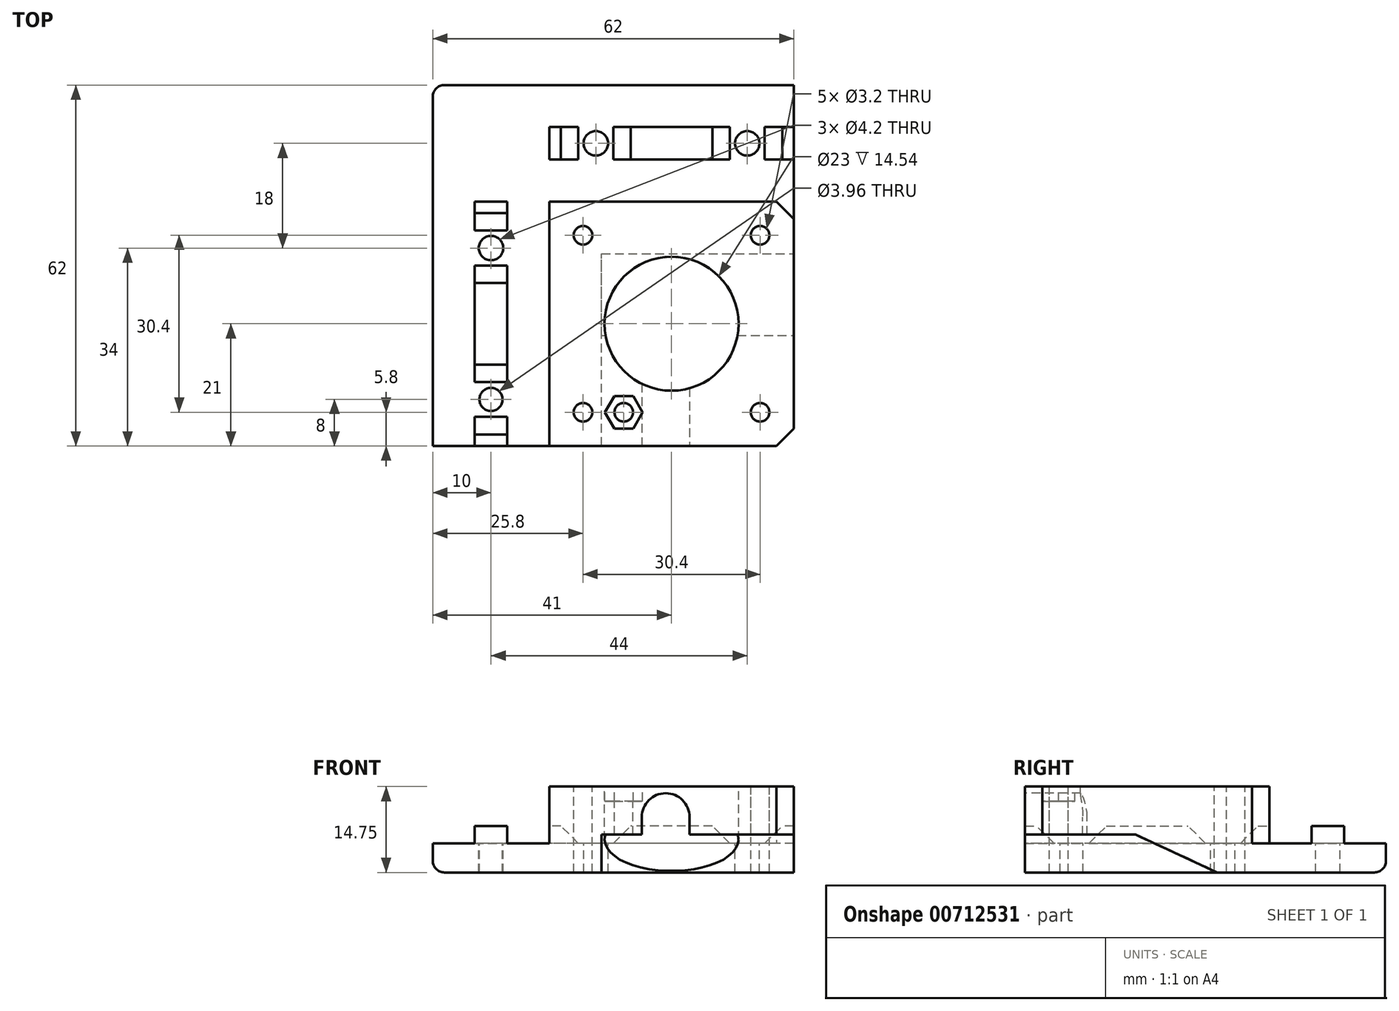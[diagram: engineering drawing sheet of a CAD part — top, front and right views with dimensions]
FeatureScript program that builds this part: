
annotation { "Feature Type Name" : "Feature", "Feature Type Description" : "" }
export const myFeature = defineFeature(function(context is Context, id is Id, definition is map)
    precondition{}
    {
        {
            var Q0;
            Q0=qCreatedBy(makeId("Top.planeOp"),FACE);
            var sketch = newSketch(context, id + "F0", { "sketchPlane" : qUnion([Q0])});
            skLineSegment(sketch, "E0.bottom", {"start": v(0, 0) * mm, "end": v(59, 0) * mm});
            skLineSegment(sketch, "E0.top", {"start": v(0, 54) * mm, "end": v(59, 54) * mm});
            skLineSegment(sketch, "E0.left", {"start": v(0, 0) * mm, "end": v(0, 54) * mm});
            skLineSegment(sketch, "E0.right", {"start": v(59, 0) * mm, "end": v(59, 54) * mm});
            skSolve(sketch);
        }
        {
            var Q0;
            Q0=makeQuery(id+"F0.imprint","IMPRINT",FACE,{"disambiguationData":[TD([[makeQuery(id+"F0.imprint","IMPRINT",EDGE,{"derivedFrom":sQuery(id+"F0.wireOp",EDGE,"E0.bottom")}),1.0]])]});
            extrude(context, id + "F1", {"entities" : qUnion([Q0]), "depth" : 5 * mm, "offsetDistance" : 25 * mm});
        }
        {
            var Q0;
            Q0=makeQuery(id+"F1.opExtrude","CAP_FACE",FACE,{"disambiguationData":[OSD([sQuery(id+"F0.wireOp",EDGE,"E0.bottom"),sQuery(id+"F0.wireOp",EDGE,"E0.top"),sQuery(id+"F0.wireOp",EDGE,"E0.left"),sQuery(id+"F0.wireOp",EDGE,"E0.right")])],"isStart":false});
            var sketch = newSketch(context, id + "F2", { "sketchPlane" : qUnion([Q0])});
            skLineSegment(sketch, "E1.bottom", {"start": v(59, 0) * mm, "end": v(17, 0) * mm});
            skLineSegment(sketch, "E1.top", {"start": v(59, 42) * mm, "end": v(17, 42) * mm});
            skLineSegment(sketch, "E1.left", {"start": v(59, 0) * mm, "end": v(59, 42) * mm});
            skLineSegment(sketch, "E1.right", {"start": v(17, 0) * mm, "end": v(17, 42) * mm});
            skSolve(sketch);
        }
        {
            var Q0;
            Q0=makeQuery(id+"F2.imprint","IMPRINT",FACE,{"disambiguationData":[TD([[makeQuery(id+"F2.imprint","IMPRINT",EDGE,{"derivedFrom":sQuery(id+"F2.wireOp",EDGE,"E1.bottom")}),1.0]])]});
            extrude(context, id + "F3", {"entities" : qUnion([Q0]), "operationType" : NewBodyOperationType.ADD, "depth" : 9.75 * mm, "offsetDistance" : 25 * mm});
        }
        {
            var Q0;
            Q0=makeQuery(id+"F3.boolean.opBoolean","MERGE",FACE,{"derivedFrom":[makeQuery(id+"F1.opExtrude","SWEPT_FACE",FACE,{"disambiguationData":[OSD([sQuery(id+"F0.wireOp",EDGE,"E0.right")])]}),makeQuery(id+"F3.opExtrude","SWEPT_FACE",FACE,{"disambiguationData":[OSD([sQuery(id+"F2.wireOp",EDGE,"E1.left")])]})]});
            var sketch = newSketch(context, id + "F4", { "sketchPlane" : qUnion([Q0])});
            skLineSegment(sketch, "E2", {"start": v(0, 0) * mm, "end": v(0, 6.5) * mm});
            skLineSegment(sketch, "E3", {"start": v(0, 6.5) * mm, "end": v(19, 6.5) * mm});
            skLineSegment(sketch, "E4", {"start": v(19, 6.5) * mm, "end": v(33, 0) * mm});
            skLineSegment(sketch, "E5", {"start": v(33, 0) * mm, "end": v(0, 0) * mm});
            skSolve(sketch);
        }
        {
            var Q0;
            Q0=makeQuery(id+"F4.imprint","IMPRINT",FACE,{"disambiguationData":[TD([[makeQuery(id+"F4.imprint","IMPRINT",EDGE,{"derivedFrom":sQuery(id+"F4.wireOp",EDGE,"E2")}),1.0]])]});
            extrude(context, id + "F5", {"entities" : qUnion([Q0]), "operationType" : NewBodyOperationType.REMOVE, "oppositeDirection" : true, "depth" : 33 * mm, "offsetDistance" : 25 * mm});
        }
        {
            var Q0;
            Q0=makeQuery(id+"F3.opExtrude","CAP_FACE",FACE,{"disambiguationData":[OSD([sQuery(id+"F2.wireOp",EDGE,"E1.bottom"),sQuery(id+"F2.wireOp",EDGE,"E1.top"),sQuery(id+"F2.wireOp",EDGE,"E1.left"),sQuery(id+"F2.wireOp",EDGE,"E1.right")])],"isStart":false});
            var sketch = newSketch(context, id + "F6", { "sketchPlane" : qUnion([Q0])});
            skCircle(sketch, "E6", {"center": v(38, 21) * mm, "radius": 11.5 * mm});
            skCircle(sketch, "E7", {"center": v(22.8, 36.2) * mm, "radius": 1.6 * mm});
            skCircle(sketch, "E8", {"center": v(53.2, 36.2) * mm, "radius": 1.6 * mm});
            skCircle(sketch, "E9", {"center": v(22.8, 5.8) * mm, "radius": 1.6 * mm});
            skCircle(sketch, "E10", {"center": v(53.2, 5.8) * mm, "radius": 1.6 * mm});
            skCircle(sketch, "E11", {"center": v(29.8, 5.8) * mm, "radius": 1.6 * mm});
            skSolve(sketch);
        }
        {
            var Q0;
            Q0=makeQuery(id+"F6.imprint","IMPRINT",FACE,{"disambiguationData":[TD([[makeQuery(id+"F6.imprint","IMPRINT",EDGE,{"derivedFrom":sQuery(id+"F6.wireOp",EDGE,"E7")}),1.0]])]});
            var Q1;
            Q1=makeQuery(id+"F6.imprint","IMPRINT",FACE,{"disambiguationData":[TD([[makeQuery(id+"F6.imprint","IMPRINT",EDGE,{"derivedFrom":sQuery(id+"F6.wireOp",EDGE,"E6")}),1.0]])]});
            var Q2;
            Q2=makeQuery(id+"F6.imprint","IMPRINT",FACE,{"disambiguationData":[TD([[makeQuery(id+"F6.imprint","IMPRINT",EDGE,{"derivedFrom":sQuery(id+"F6.wireOp",EDGE,"E8")}),1.0]])]});
            var Q3;
            Q3=makeQuery(id+"F6.imprint","IMPRINT",FACE,{"disambiguationData":[TD([[makeQuery(id+"F6.imprint","IMPRINT",EDGE,{"derivedFrom":sQuery(id+"F6.wireOp",EDGE,"E9")}),1.0]])]});
            var Q4;
            Q4=makeQuery(id+"F6.imprint","IMPRINT",FACE,{"disambiguationData":[TD([[makeQuery(id+"F6.imprint","IMPRINT",EDGE,{"derivedFrom":sQuery(id+"F6.wireOp",EDGE,"E10")}),1.0]])]});
            var Q5;
            Q5=makeQuery(id+"F6.imprint","IMPRINT",FACE,{"disambiguationData":[TD([[makeQuery(id+"F6.imprint","IMPRINT",EDGE,{"derivedFrom":sQuery(id+"F6.wireOp",EDGE,"E11")}),1.0]])]});
            extrude(context, id + "F7", {"entities" : qUnion([Q0, Q1, Q2, Q3, Q4, Q5]), "operationType" : NewBodyOperationType.REMOVE, "endBound" : BoundingType.THROUGH_ALL, "oppositeDirection" : true, "depth" : 25 * mm, "offsetDistance" : 25 * mm});
        }
        {
            var Q0;
            Q0=makeQuery(id+"F3.opExtrude","SWEPT_EDGE",EDGE,{"disambiguationData":[OSD([sQuery(id+"F0.wireOp",EDGE,"E0.right"),sQuery(id+"F2.wireOp",EDGE,"E1.top"),sQuery(id+"F2.wireOp",EDGE,"E1.left")])]});
            var Q1;
            Q1=makeQuery(id+"F3.boolean.opBoolean","MERGE",EDGE,{"derivedFrom":[makeQuery(id+"F1.opExtrude","SWEPT_EDGE",EDGE,{"disambiguationData":[OSD([sQuery(id+"F0.wireOp",EDGE,"E0.bottom"),sQuery(id+"F0.wireOp",EDGE,"E0.right")])]}),makeQuery(id+"F3.opExtrude","SWEPT_EDGE",EDGE,{"disambiguationData":[OSD([sQuery(id+"F2.wireOp",EDGE,"E1.bottom"),sQuery(id+"F2.wireOp",EDGE,"E1.left")])]})]});
            chamfer(context, id + "F8", {"entities" : qUnion([Q0, Q1]), "width" : 3 * mm, "tangentPropagation" : true});
        }
        {
            var Q0;
            Q0=makeQuery(id+"F3.opExtrude","CAP_FACE",FACE,{"disambiguationData":[OSD([sQuery(id+"F2.wireOp",EDGE,"E1.bottom"),sQuery(id+"F2.wireOp",EDGE,"E1.top"),sQuery(id+"F2.wireOp",EDGE,"E1.left"),sQuery(id+"F2.wireOp",EDGE,"E1.right")])],"isStart":false});
            var sketch = newSketch(context, id + "F9", { "sketchPlane" : qUnion([Q0])});
            skCircle(sketch, "E12.cCircle", {"center": v(29.8, 5.8) * mm, "radius": 2.8 * mm, "construction": true});
            skLineSegment(sketch, "E12.0", {"start": v(33.03, 5.8) * mm, "end": v(31.42, 3) * mm});
            skLineSegment(sketch, "E12.1", {"start": v(31.42, 3) * mm, "end": v(28.18, 3) * mm});
            skLineSegment(sketch, "E12.2", {"start": v(28.18, 3) * mm, "end": v(26.57, 5.8) * mm});
            skLineSegment(sketch, "E12.3", {"start": v(26.57, 5.8) * mm, "end": v(28.18, 8.6) * mm});
            skLineSegment(sketch, "E12.4", {"start": v(28.18, 8.6) * mm, "end": v(31.42, 8.6) * mm});
            skLineSegment(sketch, "E12.5", {"start": v(31.42, 8.6) * mm, "end": v(33.03, 5.8) * mm});
            skPoint(sketch, "E12.0.midPoint", {"position": v(32.23, 4.4) * mm});
            skSolve(sketch);
        }
        {
            var Q0;
            Q0=makeQuery(id+"F9.imprint","IMPRINT",FACE,{"disambiguationData":[TD([[makeQuery(id+"F9.imprint","IMPRINT",EDGE,{"derivedFrom":sQuery(id+"F9.wireOp",EDGE,"E12.0")}),-1.0]])]});
            extrude(context, id + "F10", {"entities" : qUnion([Q0]), "operationType" : NewBodyOperationType.REMOVE, "oppositeDirection" : true, "depth" : 2.5 * mm, "offsetDistance" : 25 * mm});
        }
        {
            var Q0;
            Q0=makeQuery(id+"F3.boolean.opBoolean","MERGE",FACE,{"derivedFrom":[makeQuery(id+"F7aVUtGTQ7vZGl7_1.boolean.opBoolean","MERGE",FACE,{"derivedFrom":[makeQuery(id+"F1.opExtrude","SWEPT_FACE",FACE,{"disambiguationData":[OSD([sQuery(id+"F0.wireOp",EDGE,"E0.bottom")])]}),makeQuery(id+"F7aVUtGTQ7vZGl7_1.opExtrude","SWEPT_FACE",FACE,{"disambiguationData":[OSD([sQuery(id+"Fs2P3l27It3FXby_1.wireOp",EDGE,"bHcCaI8n-BMMI-Yc99-4eW4-bQ5ukSnPJtkv.top")])]})]}),makeQuery(id+"F3.opExtrude","SWEPT_FACE",FACE,{"disambiguationData":[OSD([sQuery(id+"F2.wireOp",EDGE,"E1.bottom")])]})]});
            var sketch = newSketch(context, id + "F11", { "sketchPlane" : qUnion([Q0])});
            skLineSegment(sketch, "E13.top", {"start": v(32.9, 6.5) * mm, "end": v(41.1, 6.5) * mm});
            skLineSegment(sketch, "E13.left", {"start": v(32.9, 9.5) * mm, "end": v(32.9, 6.5) * mm});
            skLineSegment(sketch, "E13.right", {"start": v(41.1, 9.5) * mm, "end": v(41.1, 6.5) * mm});
            skArc(sketch, "E14.trimOffspring", {"start": v(41.1, 9.5) * mm, "mid": v(37, 13.6) * mm, "end": v(32.9, 9.5) * mm});
            skSolve(sketch);
        }
        {
            var Q0;
            Q0=makeQuery(id+"F11.imprint","IMPRINT",FACE,{"disambiguationData":[TD([[makeQuery(id+"F11.imprint","IMPRINT",EDGE,{"derivedFrom":sQuery(id+"F11.wireOp",EDGE,"E13.top")}),1.0]])]});
            extrude(context, id + "F12", {"entities" : qUnion([Q0]), "operationType" : NewBodyOperationType.REMOVE, "endBound" : BoundingType.UP_TO_NEXT, "oppositeDirection" : true, "depth" : 25 * mm, "offsetDistance" : 25 * mm});
        }
        {
            var Q0;
            Q0=makeQuery(id+"F1.opExtrude","CAP_FACE",FACE,{"disambiguationData":[OSD([sQuery(id+"F0.wireOp",EDGE,"E0.bottom"),sQuery(id+"F0.wireOp",EDGE,"E0.top"),sQuery(id+"F0.wireOp",EDGE,"E0.left"),sQuery(id+"F0.wireOp",EDGE,"E0.right")])],"isStart":false});
            var sketch = newSketch(context, id + "F13", { "sketchPlane" : qUnion([Q0])});
            skLineSegment(sketch, "E15", {"start": v(56, 42) * mm, "end": v(59, 42) * mm});
            skSolve(sketch);
        }
        {
            var Q0;
            {var subQ1=sQuery(id+"F13.wireOp",EDGE,"E15");Q0=makeQuery(id+"F13.imprint","IMPRINT",FACE,{"disambiguationData":[TD([[makeQuery(id+"F13.imprint","IMPRINT",EDGE,{"derivedFrom":subQ1}),1.0]])]});}
            extrude(context, id + "F14", {"entities" : qUnion([Q0]), "operationType" : NewBodyOperationType.REMOVE, "endBound" : BoundingType.THROUGH_ALL, "oppositeDirection" : true, "depth" : 25 * mm, "offsetDistance" : 25 * mm});
        }
        {
            var Q0;
            {var subQ0=sQuery(id+"F2.wireOp",EDGE,"E1.top");Q0=makeQuery(id+"F14.boolean.opBoolean","MERGE",FACE,{"derivedFrom":[makeQuery(id+"F3.opExtrude","SWEPT_FACE",FACE,{"disambiguationData":[OSD([subQ0])]})],"fromTools":[makeQuery(id+"F14.opExtrude","SWEPT_FACE",FACE,{"disambiguationData":[OSD([subQ0,sQuery(id+"F13.wireOp",EDGE,"E15")])]})]});}
            var sketch = newSketch(context, id + "F15", { "sketchPlane" : qUnion([Q0])});
            skLineSegment(sketch, "E16.bottom", {"start": v(-59, 5) * mm, "end": v(-17, 5) * mm});
            skLineSegment(sketch, "E16.top", {"start": v(-59, 0) * mm, "end": v(-17, 0) * mm});
            skLineSegment(sketch, "E16.left", {"start": v(-59, 5) * mm, "end": v(-59, 0) * mm});
            skLineSegment(sketch, "E16.right", {"start": v(-17, 5) * mm, "end": v(-17, 0) * mm});
            skSolve(sketch);
        }
        {
            var Q0;
            Q0=makeQuery(id+"F15.imprint","IMPRINT",FACE,{"disambiguationData":[TD([[makeQuery(id+"F15.imprint","IMPRINT",EDGE,{"derivedFrom":sQuery(id+"F15.wireOp",EDGE,"E16.top")}),1.0]])]});
            extrude(context, id + "F16", {"entities" : qUnion([Q0]), "operationType" : NewBodyOperationType.ADD, "depth" : 20 * mm, "offsetDistance" : 25 * mm});
        }
        {
            var Q0;
            {var subQ0=sQuery(id+"F2.wireOp",EDGE,"E1.right");Q0=makeQuery(id+"F16.boolean.opBoolean","MERGE",FACE,{"derivedFrom":[makeQuery(id+"F14.boolean.opBoolean","MERGE",FACE,{"derivedFrom":[makeQuery(id+"F3.opExtrude","SWEPT_FACE",FACE,{"disambiguationData":[OSD([subQ0])]})],"fromTools":[makeQuery(id+"F14.opExtrude","SWEPT_FACE",FACE,{"disambiguationData":[OSD([subQ0])]})]}),makeQuery(id+"F16.opExtrude","SWEPT_FACE",FACE,{"disambiguationData":[OSD([sQuery(id+"F15.wireOp",EDGE,"E16.right")])]})]});}
            var sketch = newSketch(context, id + "F17", { "sketchPlane" : qUnion([Q0])});
            skLineSegment(sketch, "E17.bottom", {"start": v(-62, 5) * mm, "end": v(0, 5) * mm});
            skLineSegment(sketch, "E17.top", {"start": v(-62, 0) * mm, "end": v(0, 0) * mm});
            skLineSegment(sketch, "E17.left", {"start": v(-62, 5) * mm, "end": v(-62, 0) * mm});
            skLineSegment(sketch, "E17.right", {"start": v(0, 5) * mm, "end": v(0, 0) * mm});
            skSolve(sketch);
        }
        {
            var Q0;
            Q0=makeQuery(id+"F17.imprint","IMPRINT",FACE,{"disambiguationData":[TD([[makeQuery(id+"F17.imprint","IMPRINT",EDGE,{"derivedFrom":sQuery(id+"F17.wireOp",EDGE,"E17.top")}),-1.0]])]});
            extrude(context, id + "F18", {"entities" : qUnion([Q0]), "operationType" : NewBodyOperationType.ADD, "depth" : 20 * mm, "offsetDistance" : 25 * mm});
        }
        {
            var Q0;
            Q0=makeQuery(id+"F18.opExtrude","CAP_EDGE",EDGE,{"disambiguationData":[OSD([sQuery(id+"F17.wireOp",EDGE,"E17.left")])],"isStart":false});
            var Q1;
            Q1=makeQuery(id+"F18.opExtrude","CAP_EDGE",EDGE,{"disambiguationData":[OSD([sQuery(id+"F17.wireOp",EDGE,"E17.top")])],"isStart":false});
            var Q2;
            Q2=makeQuery(id+"F18.boolean.opBoolean","MERGE",EDGE,{"derivedFrom":[makeQuery(id+"F16.opExtrude","CAP_EDGE",EDGE,{"disambiguationData":[OSD([sQuery(id+"F15.wireOp",EDGE,"E16.top")])],"isStart":false}),makeQuery(id+"F18.opExtrude","SWEPT_EDGE",EDGE,{"disambiguationData":[OSD([sQuery(id+"F17.wireOp",EDGE,"E17.top"),sQuery(id+"F17.wireOp",EDGE,"E17.left")])]})]});
            fillet(context, id + "F19", {"entities" : qUnion([Q0, Q1, Q2]), "tangentPropagation" : true, "radius" : 2 * mm, "defaultsChanged" : false, "vertexSettings" : [], "allowEdgeOverflow" : false});
        }
        {
            var Q0;
            Q0=makeQuery(id+"F18.boolean.opBoolean","MERGE",FACE,{"derivedFrom":[makeQuery(id+"F16.boolean.opBoolean","MERGE",FACE,{"derivedFrom":[makeQuery(id+"F1.opExtrude","CAP_FACE",FACE,{"disambiguationData":[OSD([sQuery(id+"F0.wireOp",EDGE,"E0.bottom"),sQuery(id+"F0.wireOp",EDGE,"E0.top"),sQuery(id+"F0.wireOp",EDGE,"E0.left"),sQuery(id+"F0.wireOp",EDGE,"E0.right")])],"isStart":false}),makeQuery(id+"F16.opExtrude","SWEPT_FACE",FACE,{"disambiguationData":[OSD([sQuery(id+"F15.wireOp",EDGE,"E16.bottom")])]})]}),makeQuery(id+"F18.opExtrude","SWEPT_FACE",FACE,{"disambiguationData":[OSD([sQuery(id+"F17.wireOp",EDGE,"E17.bottom")])]})]});
            var sketch = newSketch(context, id + "F20", { "sketchPlane" : qUnion([Q0])});
            skLineSegment(sketch, "E18.bottom", {"start": v(59, 54.8) * mm, "end": v(17, 54.8) * mm});
            skLineSegment(sketch, "E18.top", {"start": v(59, 49.2) * mm, "end": v(17, 49.2) * mm});
            skLineSegment(sketch, "E18.left", {"start": v(59, 54.8) * mm, "end": v(59, 49.2) * mm});
            skLineSegment(sketch, "E18.right", {"start": v(17, 54.8) * mm, "end": v(17, 49.2) * mm});
            skLineSegment(sketch, "E19.bottom", {"start": v(4.2, 0) * mm, "end": v(9.8, 0) * mm});
            skLineSegment(sketch, "E19.top", {"start": v(4.2, 42) * mm, "end": v(9.8, 42) * mm});
            skLineSegment(sketch, "E19.left", {"start": v(4.2, 0) * mm, "end": v(4.2, 42) * mm});
            skLineSegment(sketch, "E19.right", {"start": v(9.8, 0) * mm, "end": v(9.8, 42) * mm});
            skLineSegment(sketch, "E20.bottom", {"start": v(22, 54.8) * mm, "end": v(28, 54.8) * mm});
            skLineSegment(sketch, "E20.top", {"start": v(22, 49.2) * mm, "end": v(28, 49.2) * mm});
            skLineSegment(sketch, "E20.left", {"start": v(22, 54.8) * mm, "end": v(22, 49.2) * mm});
            skLineSegment(sketch, "E20.right", {"start": v(28, 54.8) * mm, "end": v(28, 49.2) * mm});
            skLineSegment(sketch, "E21.bottom", {"start": v(48, 54.8) * mm, "end": v(54, 54.8) * mm});
            skLineSegment(sketch, "E21.top", {"start": v(48, 49.2) * mm, "end": v(54, 49.2) * mm});
            skLineSegment(sketch, "E21.left", {"start": v(48, 54.8) * mm, "end": v(48, 49.2) * mm});
            skLineSegment(sketch, "E21.right", {"start": v(54, 54.8) * mm, "end": v(54, 49.2) * mm});
            skLineSegment(sketch, "E22.bottom", {"start": v(4.2, 37) * mm, "end": v(9.8, 37) * mm});
            skLineSegment(sketch, "E22.top", {"start": v(4.2, 31) * mm, "end": v(9.8, 31) * mm});
            skLineSegment(sketch, "E22.left", {"start": v(4.2, 37) * mm, "end": v(4.2, 31) * mm});
            skLineSegment(sketch, "E22.right", {"start": v(9.8, 37) * mm, "end": v(9.8, 31) * mm});
            skLineSegment(sketch, "E23.bottom", {"start": v(4.2, 11) * mm, "end": v(9.8, 11) * mm});
            skLineSegment(sketch, "E23.top", {"start": v(4.2, 5) * mm, "end": v(9.8, 5) * mm});
            skLineSegment(sketch, "E23.left", {"start": v(4.2, 11) * mm, "end": v(4.2, 5) * mm});
            skLineSegment(sketch, "E23.right", {"start": v(9.8, 11) * mm, "end": v(9.8, 5) * mm});
            skSolve(sketch);
        }
        {
            var Q0;
            {var subQ0=sQuery(id+"F20.wireOp",EDGE,"E22.top");Q0=makeQuery(id+"F20.imprint","IMPRINT",FACE,{"disambiguationData":[TD([[makeQuery(id+"F20.imprint","IMPRINT",EDGE,{"derivedFrom":subQ0}),-1.0]])]});}
            var Q1;
            {var subQ0=sQuery(id+"F20.wireOp",EDGE,"E19.top");Q1=makeQuery(id+"F20.imprint","IMPRINT",FACE,{"disambiguationData":[TD([[makeQuery(id+"F20.imprint","IMPRINT",EDGE,{"derivedFrom":subQ0}),-1.0]])]});}
            var Q2;
            {var subQ0=sQuery(id+"F20.wireOp",EDGE,"E19.bottom");Q2=makeQuery(id+"F20.imprint","IMPRINT",FACE,{"disambiguationData":[TD([[makeQuery(id+"F20.imprint","IMPRINT",EDGE,{"derivedFrom":subQ0}),1.0]])]});}
            var Q3;
            {var subQ0=sQuery(id+"F20.wireOp",EDGE,"E18.right");Q3=makeQuery(id+"F20.imprint","IMPRINT",FACE,{"disambiguationData":[TD([[makeQuery(id+"F20.imprint","IMPRINT",EDGE,{"derivedFrom":subQ0}),1.0]])]});}
            var Q4;
            {var subQ0=sQuery(id+"F20.wireOp",EDGE,"E20.right");Q4=makeQuery(id+"F20.imprint","IMPRINT",FACE,{"disambiguationData":[TD([[makeQuery(id+"F20.imprint","IMPRINT",EDGE,{"derivedFrom":subQ0}),1.0]])]});}
            var Q5;
            {var subQ0=sQuery(id+"F20.wireOp",EDGE,"E18.left");Q5=makeQuery(id+"F20.imprint","IMPRINT",FACE,{"disambiguationData":[TD([[makeQuery(id+"F20.imprint","IMPRINT",EDGE,{"derivedFrom":subQ0}),1.0]])]});}
            extrude(context, id + "F21", {"entities" : qUnion([Q0, Q1, Q2, Q3, Q4, Q5]), "operationType" : NewBodyOperationType.ADD, "depth" : 3 * mm, "offsetDistance" : 25 * mm});
        }
        {
            var Q0;
            Q0=makeQuery(id+"F21.opExtrude","CAP_EDGE",EDGE,{"disambiguationData":[OSD([sQuery(id+"F20.wireOp",EDGE,"E21.right")])],"isStart":false});
            var Q1;
            Q1=makeQuery(id+"F21.opExtrude","CAP_EDGE",EDGE,{"disambiguationData":[OSD([sQuery(id+"F20.wireOp",EDGE,"E21.left")])],"isStart":false});
            var Q2;
            Q2=makeQuery(id+"F21.opExtrude","CAP_EDGE",EDGE,{"disambiguationData":[OSD([sQuery(id+"F20.wireOp",EDGE,"E20.right")])],"isStart":false});
            var Q3;
            Q3=makeQuery(id+"F21.opExtrude","CAP_EDGE",EDGE,{"disambiguationData":[OSD([sQuery(id+"F20.wireOp",EDGE,"E20.left")])],"isStart":false});
            var Q4;
            Q4=makeQuery(id+"F21.opExtrude","CAP_EDGE",EDGE,{"disambiguationData":[OSD([sQuery(id+"F20.wireOp",EDGE,"E22.bottom")])],"isStart":false});
            var Q5;
            Q5=makeQuery(id+"F21.opExtrude","CAP_EDGE",EDGE,{"disambiguationData":[OSD([sQuery(id+"F20.wireOp",EDGE,"E22.top")])],"isStart":false});
            var Q6;
            Q6=makeQuery(id+"F21.opExtrude","CAP_EDGE",EDGE,{"disambiguationData":[OSD([sQuery(id+"F20.wireOp",EDGE,"E23.bottom")])],"isStart":false});
            var Q7;
            Q7=makeQuery(id+"F21.opExtrude","CAP_EDGE",EDGE,{"disambiguationData":[OSD([sQuery(id+"F20.wireOp",EDGE,"E23.top")])],"isStart":false});
            chamfer(context, id + "F22", {"entities" : qUnion([Q0, Q1, Q2, Q3, Q4, Q5, Q6, Q7]), "width" : 3 * mm, "tangentPropagation" : true});
        }
        {
            var Q0;
            Q0=makeQuery(id+"F18.boolean.opBoolean","MERGE",FACE,{"derivedFrom":[makeQuery(id+"F16.boolean.opBoolean","MERGE",FACE,{"derivedFrom":[makeQuery(id+"F1.opExtrude","CAP_FACE",FACE,{"disambiguationData":[OSD([sQuery(id+"F0.wireOp",EDGE,"E0.bottom"),sQuery(id+"F0.wireOp",EDGE,"E0.top"),sQuery(id+"F0.wireOp",EDGE,"E0.left"),sQuery(id+"F0.wireOp",EDGE,"E0.right")])],"isStart":false}),makeQuery(id+"F16.opExtrude","SWEPT_FACE",FACE,{"disambiguationData":[OSD([sQuery(id+"F15.wireOp",EDGE,"E16.bottom")])]})]}),makeQuery(id+"F18.opExtrude","SWEPT_FACE",FACE,{"disambiguationData":[OSD([sQuery(id+"F17.wireOp",EDGE,"E17.bottom")])]})]});
            var sketch = newSketch(context, id + "F23", { "sketchPlane" : qUnion([Q0])});
            skCircle(sketch, "E24", {"center": v(25, 52) * mm, "radius": 2.1 * mm});
            skCircle(sketch, "E25", {"center": v(51, 52) * mm, "radius": 2.1 * mm});
            skCircle(sketch, "E26", {"center": v(7, 34) * mm, "radius": 2.1 * mm});
            skPoint(sketch, "E26.centerSnap0", {"position": v(7, 31) * mm});
            skCircle(sketch, "E27", {"center": v(7, 8) * mm, "radius": 1.98 * mm});
            skSolve(sketch);
        }
        {
            var Q0;
            Q0=makeQuery(id+"F23.imprint","IMPRINT",FACE,{"disambiguationData":[TD([[makeQuery(id+"F23.imprint","IMPRINT",EDGE,{"derivedFrom":sQuery(id+"F23.wireOp",EDGE,"E27")}),1.0]])]});
            var Q1;
            Q1=makeQuery(id+"F23.imprint","IMPRINT",FACE,{"disambiguationData":[TD([[makeQuery(id+"F23.imprint","IMPRINT",EDGE,{"derivedFrom":sQuery(id+"F23.wireOp",EDGE,"E26")}),1.0]])]});
            var Q2;
            Q2=makeQuery(id+"F23.imprint","IMPRINT",FACE,{"disambiguationData":[TD([[makeQuery(id+"F23.imprint","IMPRINT",EDGE,{"derivedFrom":sQuery(id+"F23.wireOp",EDGE,"E24")}),1.0]])]});
            var Q3;
            Q3=makeQuery(id+"F23.imprint","IMPRINT",FACE,{"disambiguationData":[TD([[makeQuery(id+"F23.imprint","IMPRINT",EDGE,{"derivedFrom":sQuery(id+"F23.wireOp",EDGE,"E25")}),1.0]])]});
            extrude(context, id + "F24", {"entities" : qUnion([Q0, Q1, Q2, Q3]), "operationType" : NewBodyOperationType.REMOVE, "endBound" : BoundingType.THROUGH_ALL, "oppositeDirection" : true, "depth" : 25 * mm, "offsetDistance" : 25 * mm});
        }
    });
